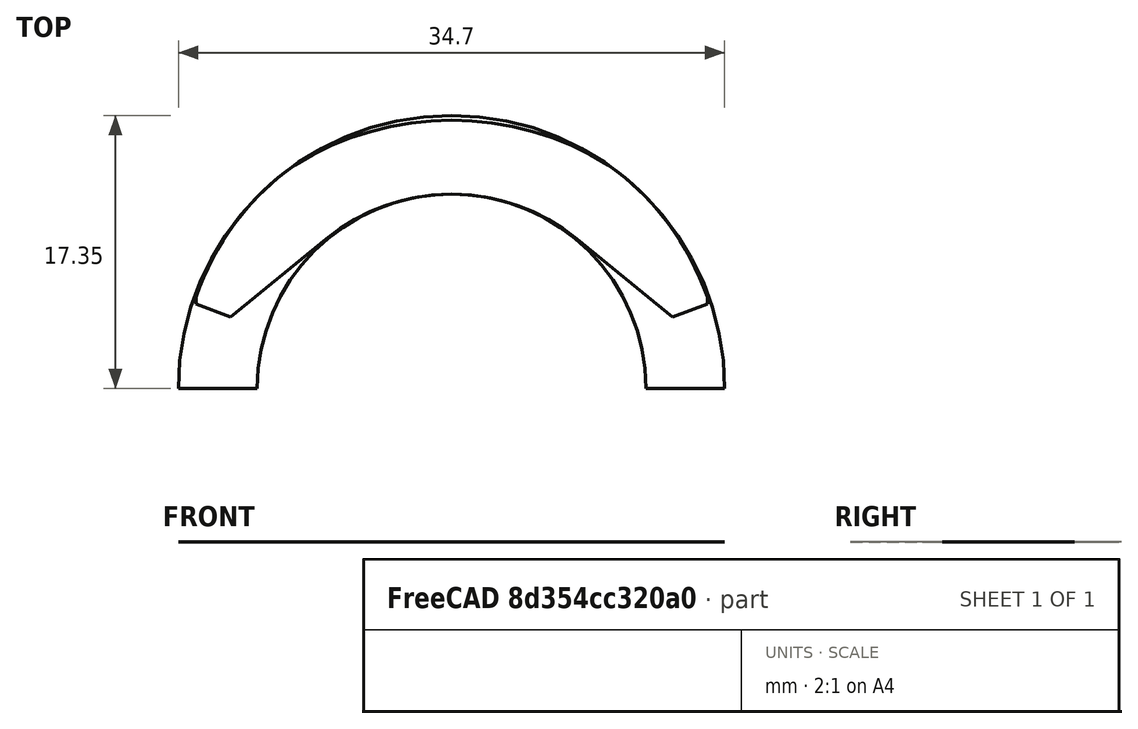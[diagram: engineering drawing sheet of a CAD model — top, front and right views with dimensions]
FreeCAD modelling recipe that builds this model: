
FCSTD DOCUMENT  (FreeCAD 0.18R4 (GitTag))
Label: rotor1
License: All rights reserved
LicenseURL: http://en.wikipedia.org/wiki/All_rights_reserved
objects: Sketcher::SketchObject×4, PartDesign::Body×2, Surface::Filling×2, Spreadsheet::Sheet×1
note: 8 computed .brp shape members not serialized (recipe doc carries the construction recipe); baked Part::Feature solids carry a one-line shape summary decoded from their .brp

FEATURE [Spreadsheet::Sheet] Spreadsheet  label="Variables"
  cells = A2=poleNumber; B2(poleNumber)=2; A3=outerDiameter; B3(outerDiameter)==innerDiameter + magnetThickness * 2; D3=Calc Value; A4=innerDiameter; B4(innerDiameter)=24.7; D4=Input Value; A5=stackLength; B5(stackLength)=20; A6=stackingFactor; B6(stackingFactor)=0.95; A7=magnetFrontAngle; B7(magnetFrontAngle)=80; A8=magnetBackAngle; B8(magnetBackAngle)=70; A9=magnetEdgeAngle; B9(magnetEdgeAngle)=20; A10=magnetCutSide; B10(magnetCutSide)=0.5; A11=magnetTopAirgap; B11(magnetTopAirgap)=0.3; A12=magnetEdgeAirgap; B12(magnetEdgeAirgap)=0.1; A13=magnetOffset; B13(magnetOffset)=0.25; A14=magnetLength; B14(magnetLength)=30; A15=magnetThickness; B15(magnetThickness)=5; A16=magnetEmbrace; B16(magnetEmbrace)=80; A17=segmentAngle; B17(segmentAngle)==360 / poleNumber
FEATURE [Sketcher::SketchObject] Sketch003  label="RotorSegment"
  MapMode = 5
  Support = -> [XY_Plane]
  expr: Constraints[6] = Variables.segmentAngle
  expr: Constraints[3] = Variables.outerDiameter
  expr: Constraints[2] = Variables.innerDiameter
  sketch-geometry (9):
    g0: Circle [constr] CenterX=0 CenterY=0 CenterZ=0 NormalX=0 NormalY=0 NormalZ=1 AngleXU=0 Radius=12.35
    g1: Circle [constr] CenterX=0 CenterY=0 CenterZ=0 NormalX=0 NormalY=0 NormalZ=1 AngleXU=0 Radius=17.35
    g2: LineSegment StartX=12.35 StartY=0 StartZ=0 EndX=17.35 EndY=-5.6e-15 EndZ=0
    g3: LineSegment StartX=-12.35 StartY=-4e-15 StartZ=0 EndX=-17.35 EndY=-5.6e-15 EndZ=0
    g4: LineSegment [constr] StartX=0 StartY=0 StartZ=0 EndX=12.35 EndY=0 EndZ=0
    g5: LineSegment [constr] StartX=0 StartY=0 StartZ=0 EndX=-12.35 EndY=-4e-15 EndZ=0
    g6: LineSegment [constr] StartX=-17.35 StartY=-5.6e-15 StartZ=0 EndX=17.35 EndY=-5.6e-15 EndZ=0
    g7: ArcOfCircle CenterX=0 CenterY=0 CenterZ=0 NormalX=0 NormalY=0 NormalZ=1 AngleXU=0 Radius=17.35 StartAngle=-6.2e-15 EndAngle=3.14159
    g8: ArcOfCircle CenterX=0 CenterY=0 CenterZ=0 NormalX=0 NormalY=0 NormalZ=1 AngleXU=0 Radius=12.35 StartAngle=0 EndAngle=3.14159
  constraints (22):
    c: Coincident(g0,g-1)
    c: Coincident(g1,g0)
    c: Diameter(g0) = 24.7
    c: Diameter(g1) = 34.7
    c: PointOnObject(g2,g0)
    c: PointOnObject(g2,g1)
    c: Angle(g2,g3) = 3.14159
    c: Coincident(g4,g-1)
    c: Coincident(g4,g2)
    c: Coincident(g5,g4)
    c: Coincident(g5,g3)
    c: Parallel(g4,g2)
    c: Parallel(g5,g3)
    c: Coincident(g6,g3)
    c: Coincident(g6,g2)
    c: Coincident(g7,g-1)
    c: Coincident(g7,g2)
    c: Coincident(g7,g3)
    c: Coincident(g8,g7)
    c: Coincident(g8,g3)
    c: Coincident(g8,g2)
    c: Horizontal(g6)
FEATURE [Sketcher::SketchObject] Sketch  label="MagnetSegment"
  MapMode = 5
  Support = -> [XY_Plane]
  expr: Constraints[67] = Variables.magnetEdgeAngle
  expr: Constraints[71] = Variables.magnetCutSide
  expr: Constraints[58] = Variables.magnetEdgeAngle
  expr: Constraints[43] = Variables.segmentAngle * Variables.magnetEmbrace / 100
  expr: Constraints[31] = Variables.magnetTopAirgap
  expr: Constraints[23] = Variables.magnetBackAngle
  expr: Constraints[12] = Variables.magnetFrontAngle
  expr: Constraints[1] = Variables.innerDiameter
  expr: Constraints[85] = Variables.magnetEdgeAirgap
  expr: Constraints[62] = Variables.magnetCutSide
  expr: Constraints[6] = Variables.magnetOffset
  expr: Constraints[5] = Variables.innerDiameter + Variables.magnetOffset * 2
  expr: Constraints[3] = Variables.outerDiameter
  sketch-geometry (35):
    g0: Circle [constr] CenterX=0 CenterY=0 CenterZ=0 NormalX=0 NormalY=0 NormalZ=1 AngleXU=0 Radius=12.35
    g1: Circle [constr] CenterX=0 CenterY=0 CenterZ=0 NormalX=0 NormalY=0 NormalZ=1 AngleXU=0 Radius=17.35
    g2: Circle [constr] CenterX=0 CenterY=-0.25 CenterZ=0 NormalX=0 NormalY=0 NormalZ=1 AngleXU=0 Radius=12.6
    g3: LineSegment [constr] StartX=0 StartY=0 StartZ=0 EndX=-7.97536 EndY=9.50467 EndZ=0
    g4: LineSegment [constr] StartX=-7.97536 StartY=9.50467 StartZ=0 EndX=7.97536 EndY=9.50467 EndZ=0
    g5: LineSegment [constr] StartX=7.97536 StartY=9.50467 StartZ=0 EndX=0 EndY=0 EndZ=0
    g6: ArcOfCircle CenterX=0 CenterY=-0.25 CenterZ=0 NormalX=0 NormalY=0 NormalZ=1 AngleXU=0 Radius=12.6 StartAngle=0.885419 EndAngle=2.25617
    g7: LineSegment [constr] StartX=0 StartY=0 StartZ=0 EndX=-9.95155 EndY=14.2123 EndZ=0
    g8: LineSegment [constr] StartX=-9.95155 StartY=14.2123 StartZ=0 EndX=9.95155 EndY=14.2123 EndZ=0
    g9: LineSegment [constr] StartX=9.95155 StartY=14.2123 StartZ=0 EndX=0 EndY=0 EndZ=0
    g10: ArcOfCircle CenterX=0 CenterY=-1.81837 CenterZ=0 NormalX=0 NormalY=0 NormalZ=1 AngleXU=0 Radius=18.8684 StartAngle=1.01524 EndAngle=2.12636
    g11: LineSegment [constr] StartX=0 StartY=17.35 StartZ=0 EndX=0 EndY=17.05 EndZ=0
    g12: LineSegment StartX=-7.97536 StartY=9.50467 StartZ=0 EndX=-14.0263 EndY=4.55742 EndZ=0
    g13: LineSegment [constr] StartX=0 StartY=0 StartZ=0 EndX=-14.0263 EndY=4.55742 EndZ=0
    g14: LineSegment StartX=7.97536 StartY=9.50467 StartZ=0 EndX=14.0263 EndY=4.55742 EndZ=0
    g15: LineSegment [constr] StartX=-14.0263 StartY=4.55742 StartZ=0 EndX=14.0263 EndY=4.55742 EndZ=0
    g16: LineSegment [constr] StartX=0 StartY=0 StartZ=0 EndX=14.0263 EndY=4.55742 EndZ=0
    g17: LineSegment [constr] StartX=-14.0263 StartY=4.55742 StartZ=0 EndX=-16.5008 EndY=5.36144 EndZ=0
    g18: LineSegment [constr] StartX=14.0263 StartY=4.55742 StartZ=0 EndX=16.5008 EndY=5.36144 EndZ=0
    g19: LineSegment [constr] StartX=-14.0263 StartY=4.55742 StartZ=0 EndX=-16.7407 EndY=4.55742 EndZ=0
    g20: LineSegment [constr] StartX=14.0263 StartY=4.55742 StartZ=0 EndX=16.7407 EndY=4.55742 EndZ=0
    g21: LineSegment [constr] StartX=-14.0263 StartY=4.55742 StartZ=0 EndX=-16.4725 EndY=5.44778 EndZ=0
    g22: LineSegment [constr] StartX=-16.2407 StartY=5.36341 StartZ=0 EndX=-16.2407 EndY=4.55742 EndZ=0
    g23: LineSegment StartX=-14.0263 StartY=4.55742 StartZ=0 EndX=-16.2407 EndY=5.36341 EndZ=0
    g24: LineSegment [constr] StartX=14.0263 StartY=4.55742 StartZ=0 EndX=16.4725 EndY=5.44778 EndZ=0
    g25: LineSegment [constr] StartX=16.2407 StartY=4.55742 StartZ=0 EndX=16.2407 EndY=5.36341 EndZ=0
    g26: LineSegment StartX=14.0263 StartY=4.55742 StartZ=0 EndX=16.2407 EndY=5.36341 EndZ=0
    g27: LineSegment [constr] StartX=16.2407 StartY=5.36341 StartZ=0 EndX=16.2407 EndY=6.10417 EndZ=0
    g28: LineSegment [constr] StartX=-16.2407 StartY=5.36341 StartZ=0 EndX=-16.2407 EndY=6.10417 EndZ=0
    g29: LineSegment StartX=16.2407 StartY=5.36341 StartZ=0 EndX=16.2407 EndY=5.81385 EndZ=0
    g30: LineSegment [constr] StartX=16.2407 StartY=5.81385 StartZ=0 EndX=16.3349 EndY=5.84755 EndZ=0
    g31: ArcOfCircle CenterX=0 CenterY=0.205991 CenterZ=0 NormalX=0 NormalY=0 NormalZ=1 AngleXU=0 Radius=17.1817 StartAngle=0.332478 EndAngle=0.953054
    g32: LineSegment [constr] StartX=16.2407 StartY=5.81385 StartZ=0 EndX=-16.2407 EndY=5.81385 EndZ=0
    g33: ArcOfCircle CenterX=0 CenterY=0.205991 CenterZ=0 NormalX=0 NormalY=0 NormalZ=1 AngleXU=0 Radius=17.1817 StartAngle=2.18854 EndAngle=2.80911
    g34: LineSegment StartX=-16.2407 StartY=5.36341 StartZ=0 EndX=-16.2407 EndY=5.81385 EndZ=0
  constraints (97):
    c: Coincident(g0,g-1)
    c: Diameter(g0) = 24.7
    c: Coincident(g1,g0)
    c: Diameter(g1) = 34.7
    c: PointOnObject(g2,g-2)
    c: Diameter(g2) = 25.2
    c: DistanceY(g2,g-1) = 0.25
    c: Coincident(g3,g-1)
    c: PointOnObject(g3,g2)
    c: Coincident(g4,g3)
    c: Horizontal(g4)
    c: Coincident(g5,g4)
    c: Angle(g5,g3) = 1.39626
    c: Coincident(g5,g-1)
    c: Coincident(g6,g2)
    c: Coincident(g6,g3)
    c: Coincident(g6,g4)
    c: Coincident(g7,g-1)
    c: PointOnObject(g7,g1)
    c: Coincident(g8,g7)
    c: Horizontal(g8)
    c: Coincident(g9,g8)
    c: Coincident(g9,g-1)
    c: Angle(g9,g7) = 1.22173
    c: PointOnObject(g10,g-2)
    c: Coincident(g10,g7)
    c: Coincident(g10,g8)
    c: PointOnObject(g11,g-2)
    c: PointOnObject(g11,g10)
    c: Vertical(g11)
    c: PointOnObject(g11,g1)
    c: DistanceY(g11,g11) = 0.3
    c: Tangent(g12,g2)
    c: Coincident(g12,g6)
    c: Coincident(g13,g-1)
    c: Coincident(g13,g12)
    c: Coincident(g14,g6)
    c: Tangent(g14,g2)
    c: Coincident(g15,g12)
    c: Coincident(g15,g14)
    c: Horizontal(g15)
    c: Coincident(g16,g-1)
    c: Coincident(g16,g14)
    c: Angle(g16,g13) = 2.51327
    c: Coincident(g17,g12)
    c: PointOnObject(g17,g1)
    c: Parallel(g13,g17)
    c: Coincident(g18,g14)
    c: PointOnObject(g18,g1)
    c: Parallel(g16,g18)
    c: Coincident(g19,g12)
    c: PointOnObject(g19,g1)
    c: Horizontal(g19)
    c: Coincident(g20,g14)
    c: PointOnObject(g20,g1)
    c: Horizontal(g20)
    c: Coincident(g21,g12)
    c: PointOnObject(g21,g1)
    c: Angle(g21,g19) = 0.349066
    c: PointOnObject(g22,g21)
    c: PointOnObject(g22,g19)
    c: Vertical(g22)
    c: DistanceX(g19,g22) = 0.5
    c: Coincident(g23,g12)
    c: Coincident(g23,g22)
    c: Coincident(g24,g14)
    c: PointOnObject(g24,g1)
    c: Angle(g20,g24) = 0.349066
    c: PointOnObject(g25,g20)
    c: PointOnObject(g25,g24)
    c: Vertical(g25)
    c: DistanceX(g25,g20) = 0.5
    c: Coincident(g26,g14)
    c: Coincident(g26,g25)
    c: Coincident(g27,g26)
    c: PointOnObject(g27,g1)
    c: Vertical(g27)
    c: Coincident(g28,g23)
    c: PointOnObject(g28,g1)
    c: Vertical(g28)
    c: Coincident(g29,g26)
    c: PointOnObject(g29,g27)
    c: Coincident(g30,g29)
    c: PointOnObject(g30,g1)
    c: Perpendicular(g1,g30)
    c: Distance(g30) = 0.1
    c: Coincident(g31,g10)
    c: Coincident(g31,g29)
    c: PointOnObject(g31,g-2)
    c: PointOnObject(g32,g28)
    c: Horizontal(g32)
    c: Coincident(g32,g29)
    c: Coincident(g33,g10)
    c: Coincident(g33,g32)
    c: PointOnObject(g33,g-2)
    c: Coincident(g34,g23)
    c: Coincident(g34,g33)
FEATURE [Sketcher::SketchObject] Sketch004  label="BoundingBox"
  MapMode = 5
  Support = -> [XY_Plane]
  expr: Constraints[8] = Variables.outerDiameter
  sketch-geometry (6):
    g0: LineSegment StartX=-17.35 StartY=-17.35 StartZ=0 EndX=17.35 EndY=-17.35 EndZ=0
    g1: LineSegment StartX=17.35 StartY=-17.35 StartZ=0 EndX=17.35 EndY=17.35 EndZ=0
    g2: LineSegment StartX=17.35 StartY=17.35 StartZ=0 EndX=-17.35 EndY=17.35 EndZ=0
    g3: LineSegment StartX=-17.35 StartY=17.35 StartZ=0 EndX=-17.35 EndY=-17.35 EndZ=0
    g4: LineSegment [constr] StartX=-17.35 StartY=-17.35 StartZ=0 EndX=17.35 EndY=17.35 EndZ=0
    g5: GeomPoint X=0 Y=0 Z=0
  constraints (14):
    c: Coincident(g0,g1)
    c: Coincident(g1,g2)
    c: Coincident(g2,g3)
    c: Coincident(g3,g0)
    c: Horizontal(g0)
    c: Horizontal(g2)
    c: Vertical(g1)
    c: Vertical(g3)
    c: DistanceY(g1,g1) = 34.7
    c: Equal(g2,g1)
    c: Coincident(g4,g0)
    c: Coincident(g4,g1)
    c: Symmetric(g0,g1,g5)
    c: Coincident(g-1,g5)
FEATURE [PartDesign::Body] Body  label="TopView"
  Group = -> [Sketch003,Sketch,Sketch004]
  Origin = -> Origin
FEATURE [Sketcher::SketchObject] Sketch005  label="MagnetSide"
  MapMode = 5
  Support = -> [XY_Plane001]
  expr: Constraints[21] = Variables.innerDiameter / 2
  expr: Constraints[10] = Variables.outerDiameter / 2
  expr: Constraints[9] = Variables.innerDiameter / 2
  expr: Constraints[8] = Variables.magnetLength
  sketch-geometry (8):
    g0: LineSegment StartX=-15 StartY=12.35 StartZ=0 EndX=15 EndY=12.35 EndZ=0
    g1: LineSegment StartX=15 StartY=12.35 StartZ=0 EndX=15 EndY=17.35 EndZ=0
    g2: LineSegment StartX=15 StartY=17.35 StartZ=0 EndX=-15 EndY=17.35 EndZ=0
    g3: LineSegment StartX=-15 StartY=17.35 StartZ=0 EndX=-15 EndY=12.35 EndZ=0
    g4: LineSegment StartX=-15 StartY=-12.35 StartZ=0 EndX=15 EndY=-12.35 EndZ=0
    g5: LineSegment StartX=15 StartY=-12.35 StartZ=0 EndX=15 EndY=-17.35 EndZ=0
    g6: LineSegment StartX=15 StartY=-17.35 StartZ=0 EndX=-15 EndY=-17.35 EndZ=0
    g7: LineSegment StartX=-15 StartY=-17.35 StartZ=0 EndX=-15 EndY=-12.35 EndZ=0
  constraints (22):
    c: Coincident(g0,g1)
    c: Coincident(g1,g2)
    c: Coincident(g2,g3)
    c: Coincident(g3,g0)
    c: Horizontal(g0)
    c: Vertical(g1)
    c: Vertical(g3)
    c: Symmetric(g2,g1,g-2)
    c: DistanceX(g2,g2) = 30
    c: DistanceY(g-1,g0) = 12.35
    c: DistanceY(g-1,g1) = 17.35
    c: Coincident(g4,g5)
    c: Coincident(g5,g6)
    c: Coincident(g6,g7)
    c: Coincident(g7,g4)
    c: Horizontal(g4)
    c: Vertical(g5)
    c: Vertical(g7)
    c: Equal(g4,g0)
    c: Symmetric(g6,g5,g-2)
    c: Equal(g7,g3)
    c: DistanceY(g4,g-1) = 12.35
FEATURE [PartDesign::Body] Body001  label="SideView"
  Group = -> [Sketch005]
  Origin = -> Origin001
FEATURE [Surface::Filling] Surface  label="Magnet_Surface"
  Anisotropy = false
  BoundaryEdges = -> [Sketch]
  BoundaryOrder = [0,0,0,0,0,0,0,0,0,0]
  Degree = 3
  Iterations = 2
  MaximumDegree = 8
  MaximumSegments = 9
  PointsOnCurve = 15
  TolAngular = 0.01
  TolCurvature = 0.1
  Tolerance2d = 1e-05
  Tolerance3d = 0.0001
FEATURE [Surface::Filling] Surface001  label="Rotor_Surface"
  Anisotropy = false
  BoundaryEdges = -> [Sketch003]
  BoundaryOrder = [0,0,0,0]
  Degree = 3
  Iterations = 2
  MaximumDegree = 8
  MaximumSegments = 9
  PointsOnCurve = 15
  TolAngular = 0.01
  TolCurvature = 0.1
  Tolerance2d = 1e-05
  Tolerance3d = 0.0001
